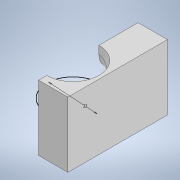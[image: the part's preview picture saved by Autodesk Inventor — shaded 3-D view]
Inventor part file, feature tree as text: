
AUTODESK INVENTOR PART (.ipt)
format: ipt  version: 2022 (Build 260153000, 153)  size: 152,064 bytes
history: native  units: mm
features: sketch x3, extrude x3, split x1, boolean_combine x1, fillet x1
ambient origin geometry x8: Origin, YZ Plane, XZ Plane, XY Plane, X Axis, Y Axis, Z Axis, Center Point
bodies: Solid1 (feature_tree), Solid2 (feature_tree)
feature tree (9):
  sketch  "Sketch1"  dims[d0=32.0mm d1=40.0mm d2=0.0mm]
  extrude  "Extrusion1"  Depth=40.0mm TaperAngle=0.0deg
  extrude  "Extrusion2"  Depth=40.0mm TaperAngle=0.0deg
  split  "Split1"
  extrude  "Extrusion3"  Depth=40.0mm
  boolean_combine  "Combine1"
  fillet  "Fillet1"  Radius=61.0mm
  sketch  "Sketch2"  dims[d3=10.0mm d4=40.0mm d5=0.0mm]
  sketch  "Sketch3"  dims[d8=18.0mm d9=0.0mm d10=40.0mm d11=61.0mm d12=10.0mm]
